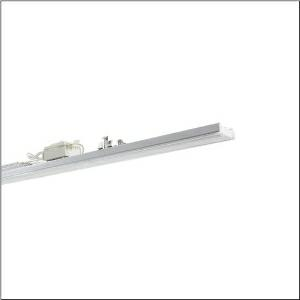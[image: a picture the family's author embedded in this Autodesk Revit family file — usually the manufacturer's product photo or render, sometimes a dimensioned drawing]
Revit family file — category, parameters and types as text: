
# Revit family: licross_11_recessed_mo_51te197n485g
name_source: partatom
category: Lighting Fixtures
units: mm (PartAtom-declared; Revit-internal decimal feet)

## family parameters
Cut with Voids When Loaded = No
Host = Face
Light Source = No
Part Type = Normal
Room Calculation Point = No
Round Connector Dimension = Use Diameter
Shared = No

## types (1)
- Licross 11 Recessed MO (1 x LED, 8580 lm, 48.5 W, 4000K)
    Apparent Load = 49 VA
    CIE Flux Codes = 55 90 98 100 100
    Color Rendering = 80
    Color Temperature = 4000K
    Default Elevation = 1800 mm
    Description = Licross 11 Recessed MO, luminaire insert, of sheet steel, galvanised, coil coated, white, length: 1.500mm, width: 66mm, height: 67mm, LED rated luminous flux: 8.580lm, light colour: 840, SDCM (Standard Deviation of Colour Matching)MacAdam ≤ 2 SDCM (initial), control gear: ON/OFF, with plug, 3-pole, with phase selection, mains connection: 220..240V, AC, 50/60Hz, rated input power: 49W, internal wiring halogen-free, primary light control with lens, of plastic, primary optical cover: cover, of PMMA, light emission: direct distribution, primary light characteristic: double asymmetric, protection rating (complete): IP54, insulation class (complete): insulation class I (protective earthing), certification: CE, ENEC, VDE, UKCA, protection symbol: D if used in an environment with non-conductive dust loads with corresponding accessories, impact resistance: IK06, permissible ambient temperature for indoor applications: -35..+35°C, corresponds to IFS (International Featured Standards) requirements for safety and quality in the food industry, reducing of maximum allowable ambient temperature of 5°C with ceiling mounting, The light source and the operating device comply with the requirements of the Ecodesign Regulation (EU) 2019/2020 and are replaceable in accordance with this regulation, packaging unit: 1 piece
    Height = 58 mm
    Lamp = 1 x LED
    Lamp Light Flux = 8580 lm
    Lamp Power = 48.5 W
    Lamp count = 1
    Length = 1500 mm
    Luminous efficacy = 177 lm/W
    Manufacturer = Siteco
    ModVariant = No
    Model = 51TE197N485G
    Mounting Place = Ceiling
    Mounting Type = Pendant
    Number of Poles = 1
    OnlyDefault = Yes
    Power Factor = 1
    Product Name = Licross 11 Recessed MO
    Product group = luminaire insert | ceiling pendant
    ProductGroupID = 901
    Protection Class = Protection class I
    Protection Degree = IP 54
    RLX_Detail_Level = 1
    RLX_Emergency_Light_Flux = 0 lm
    RLX_Emergency_Type = 0
    RLX_Emergency_Type_DB = No
    RlxData = <blob elided: 21113 chars, md5=94ab3a49>
    Socket = socket
    Standby Power = 0 W
    System Light Flux = 8580 lm
    System Power = 49 W
    Type Comments = Product without accessories
    Type Image = l_1296930.jpg
    URL = http://relux.com
    VarID = ---
    Voltage = 0 V
    Weight = 0.00 kg
    Width = 66 mm

## geometry (parser evidence)
native form markers: Blend x4, Sweep x9
no freeform markers — native parametric forms only
